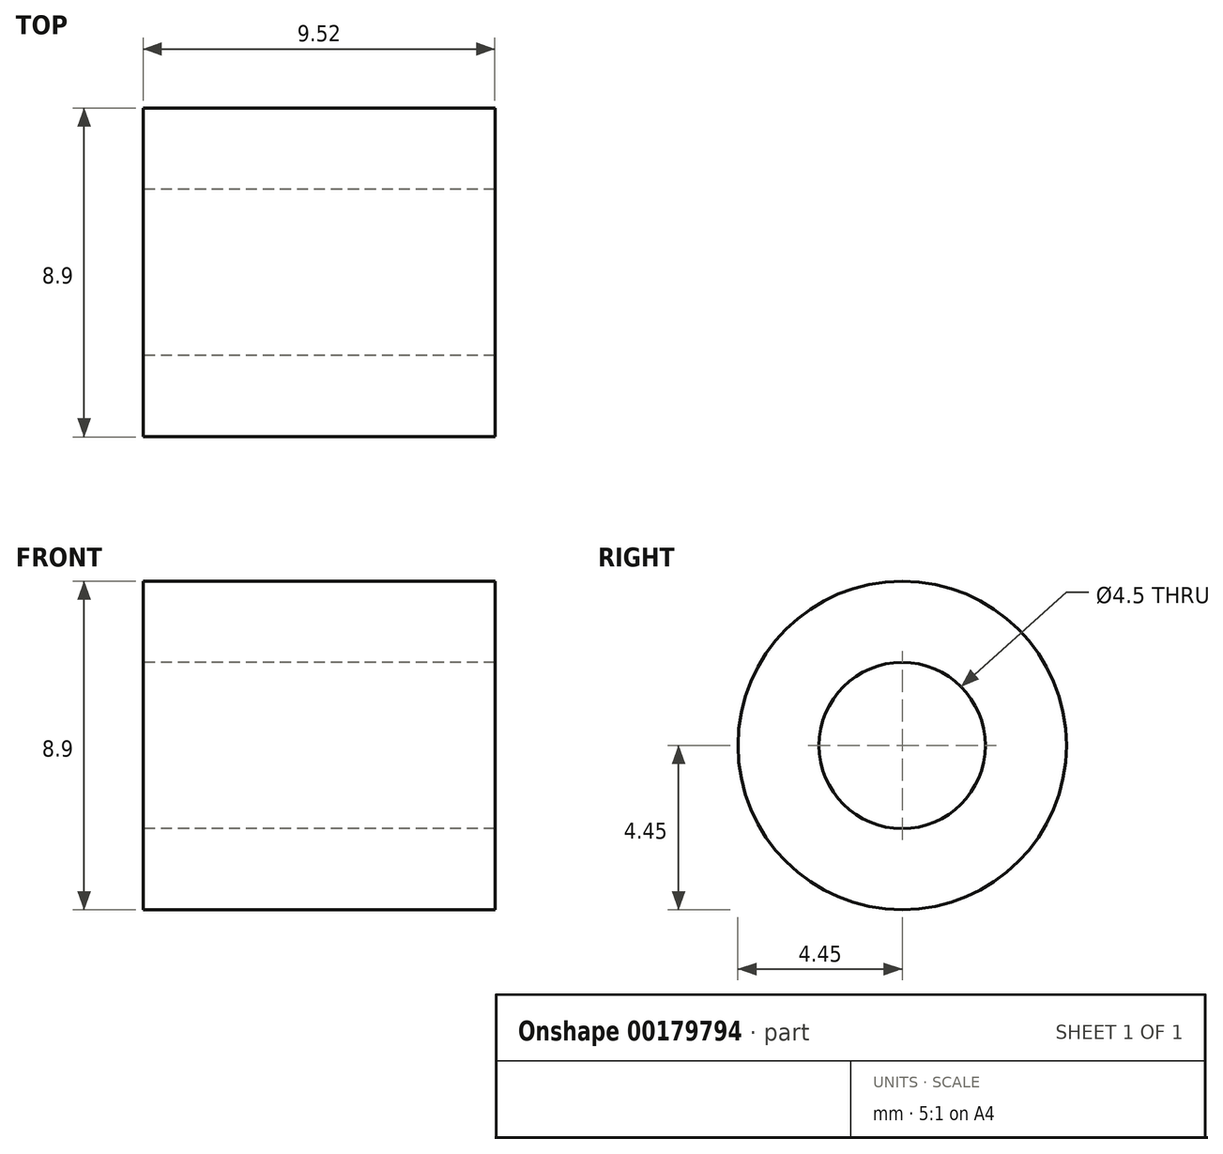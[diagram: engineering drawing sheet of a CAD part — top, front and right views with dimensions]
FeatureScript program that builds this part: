
annotation { "Feature Type Name" : "Feature", "Feature Type Description" : "" }
export const myFeature = defineFeature(function(context is Context, id is Id, definition is map)
    precondition{}
    {
        {
            var Q0;
            Q0=qCreatedBy(makeId("Right.planeOp"),FACE);
            var sketch = newSketch(context, id + "F0", { "sketchPlane" : qUnion([Q0])});
            skCircle(sketch, "E0", {"center": v(0, 0) * mm, "radius": 2.25 * mm});
            skCircle(sketch, "E1", {"center": v(0, 0) * mm, "radius": 4.45 * mm});
            skSolve(sketch);
        }
        {
            var Q0;
            Q0=makeQuery(id+"F0.imprint","IMPRINT",FACE,{"disambiguationData":[TD([[makeQuery(id+"F0.imprint","IMPRINT",EDGE,{"derivedFrom":sQuery(id+"F0.wireOp",EDGE,"E0")}),-1.0]])]});
            extrude(context, id + "F1", {"entities" : qUnion([Q0]), "endBound" : BoundingType.SYMMETRIC, "depth" : 9.52 * mm});
        }
    });
